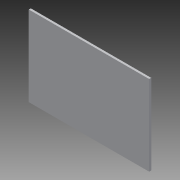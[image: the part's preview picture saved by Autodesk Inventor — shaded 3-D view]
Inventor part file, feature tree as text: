
AUTODESK INVENTOR PART (.ipt)
format: ipt  version: 2013 (Build 170138000, 138)  size: 75,264 bytes
history: native  units: mm
features: other x1, extrude x1, sketch x1
ambient origin geometry x8: Origin, YZ Plane, XZ Plane, XY Plane, X Axis, Y Axis, Z Axis, Center Point
bodies: Solid1 (feature_tree)
feature tree (3):
  other  "<userpath>\Desktop\Proyecto computacion\Modelado\Puente inventor.xlsx"
  extrude  "Extrusion1"  [1 undecoded]
  sketch  "Sketch1"  dims[d3=0.0mm]
note: 1 required parameter value undecoded (feature->parameter linkage not recoverable at this tier; creation-order binding heuristic only, values carry confidence <= 0.55)
